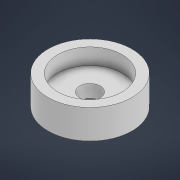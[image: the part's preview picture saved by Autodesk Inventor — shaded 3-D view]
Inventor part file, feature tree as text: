
AUTODESK INVENTOR PART (.ipt)
format: ipt  version: 2021 (Build 250183000, 183)  size: 110,080 bytes
history: native  units: mm
features: extrude x3, sketch x3
ambient origin geometry x8: Origin, YZ Plane, XZ Plane, XY Plane, X Axis, Y Axis, Z Axis, Center Point
bodies: Volumenkörper1 (feature_tree)
feature tree (6):
  extrude  "Extrusion1"  Depth=2.0mm TaperAngle=0.0deg
  extrude  "Extrusion2"  Depth=10.0mm
  extrude  "Extrusion3"  Depth=2.5mm
  sketch  "Skizze1"  dims[d0=13.0mm d1=2.0mm d2=0.0mm]
  sketch  "Skizze2"  dims[d3=10.0mm d4=13.0mm]
  sketch  "Skizze3"  dims[d5=2.5mm d6=0.0mm d7=3.2mm d8=2.5mm d9=0.0mm]
